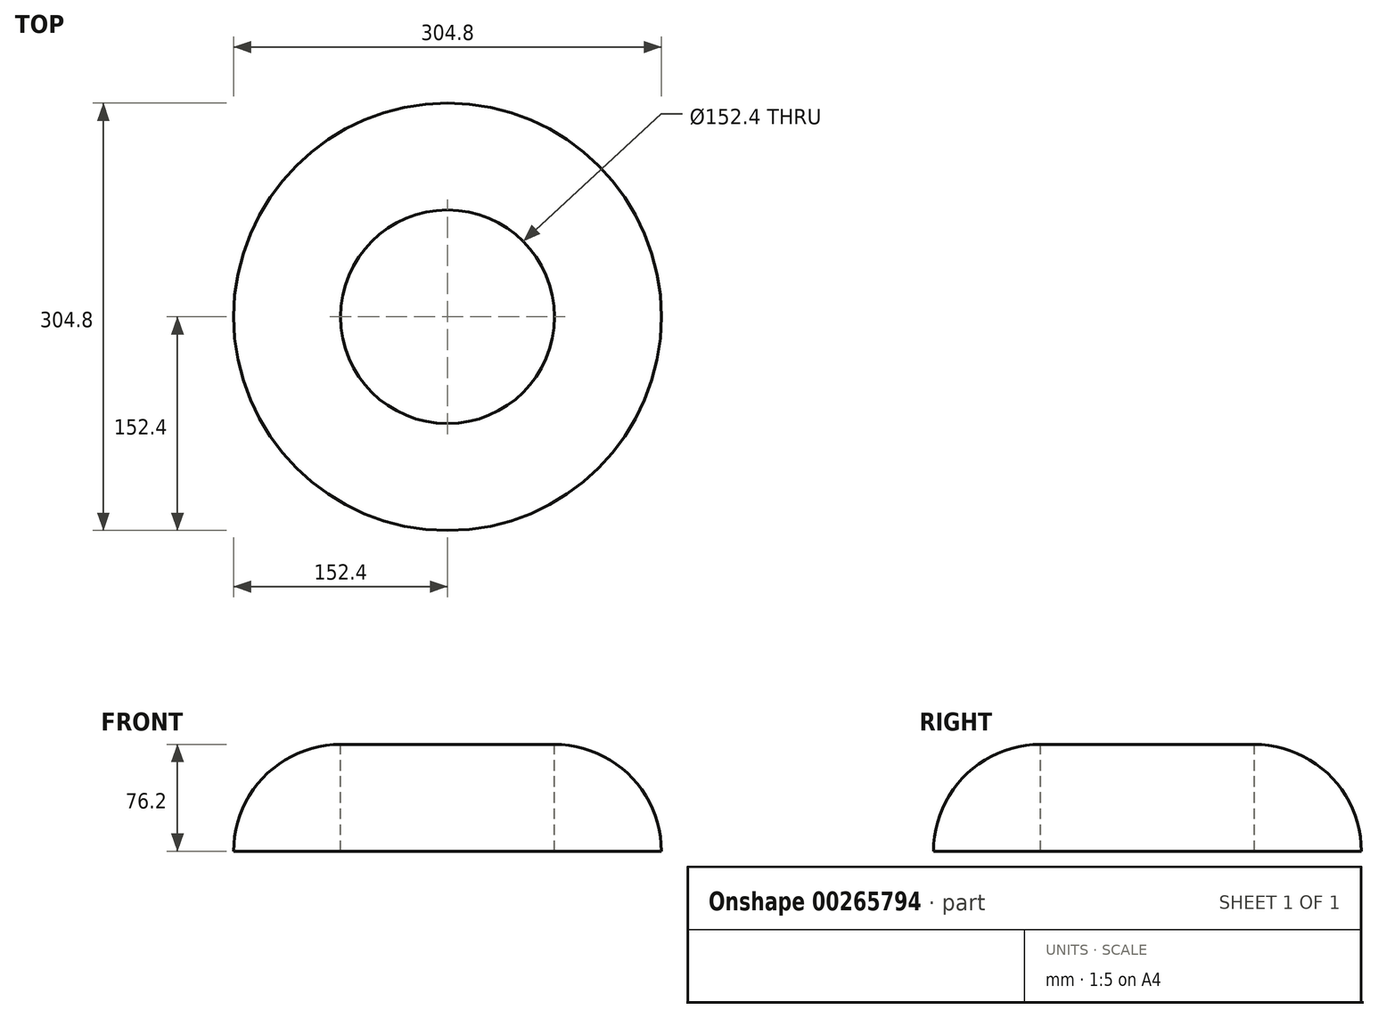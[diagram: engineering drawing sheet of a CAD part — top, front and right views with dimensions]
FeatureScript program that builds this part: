
annotation { "Feature Type Name" : "Feature", "Feature Type Description" : "" }
export const myFeature = defineFeature(function(context is Context, id is Id, definition is map)
    precondition{}
    {
        {
            var Q0;
            Q0=qCreatedBy(makeId("Front.planeOp"),FACE);
            var sketch = newSketch(context, id + "F0", { "sketchPlane" : qUnion([Q0])});
            skLineSegment(sketch, "E0", {"start": v(0, 0) * mm, "end": v(76.2, 0) * mm});
            skArc(sketch, "E1", {"start": v(76.2, 0) * mm, "mid": v(0, 76.2) * mm, "end": v(-76.2, 0) * mm});
            skLineSegment(sketch, "E2", {"start": v(76.2, 0) * mm, "end": v(76.2, -76.2) * mm});
            skLineSegment(sketch, "E3", {"start": v(-76.2, 0) * mm, "end": v(76.2, -76.2) * mm});
            skLineSegment(sketch, "E4", {"start": v(0, 0) * mm, "end": v(-76.2, 0) * mm});
            skLineSegment(sketch, "E5", {"start": v(0, 0) * mm, "end": v(0, 76.2) * mm});
            skLineSegment(sketch, "E6", {"start": v(0, 0) * mm, "end": v(76.2, -76.2) * mm});
            skSolve(sketch);
        }
        {
            var Q0;
            {var subQ0=sQuery(id+"F0.wireOp",EDGE,"E4");Q0=makeQuery(id+"F0.imprint","IMPRINT",FACE,{"disambiguationData":[TD([[makeQuery(id+"F0.imprint","IMPRINT",EDGE,{"derivedFrom":subQ0}),-1.0]])]});}
            var Q1;
            Q1=sQuery(id+"F0.wireOp",EDGE,"E2");
            revolve(context, id + "F1", {"entities" : qUnion([Q0]), "axis" : qUnion([Q1]), "revolveType" : RevolveType.FULL});
        }
    });
